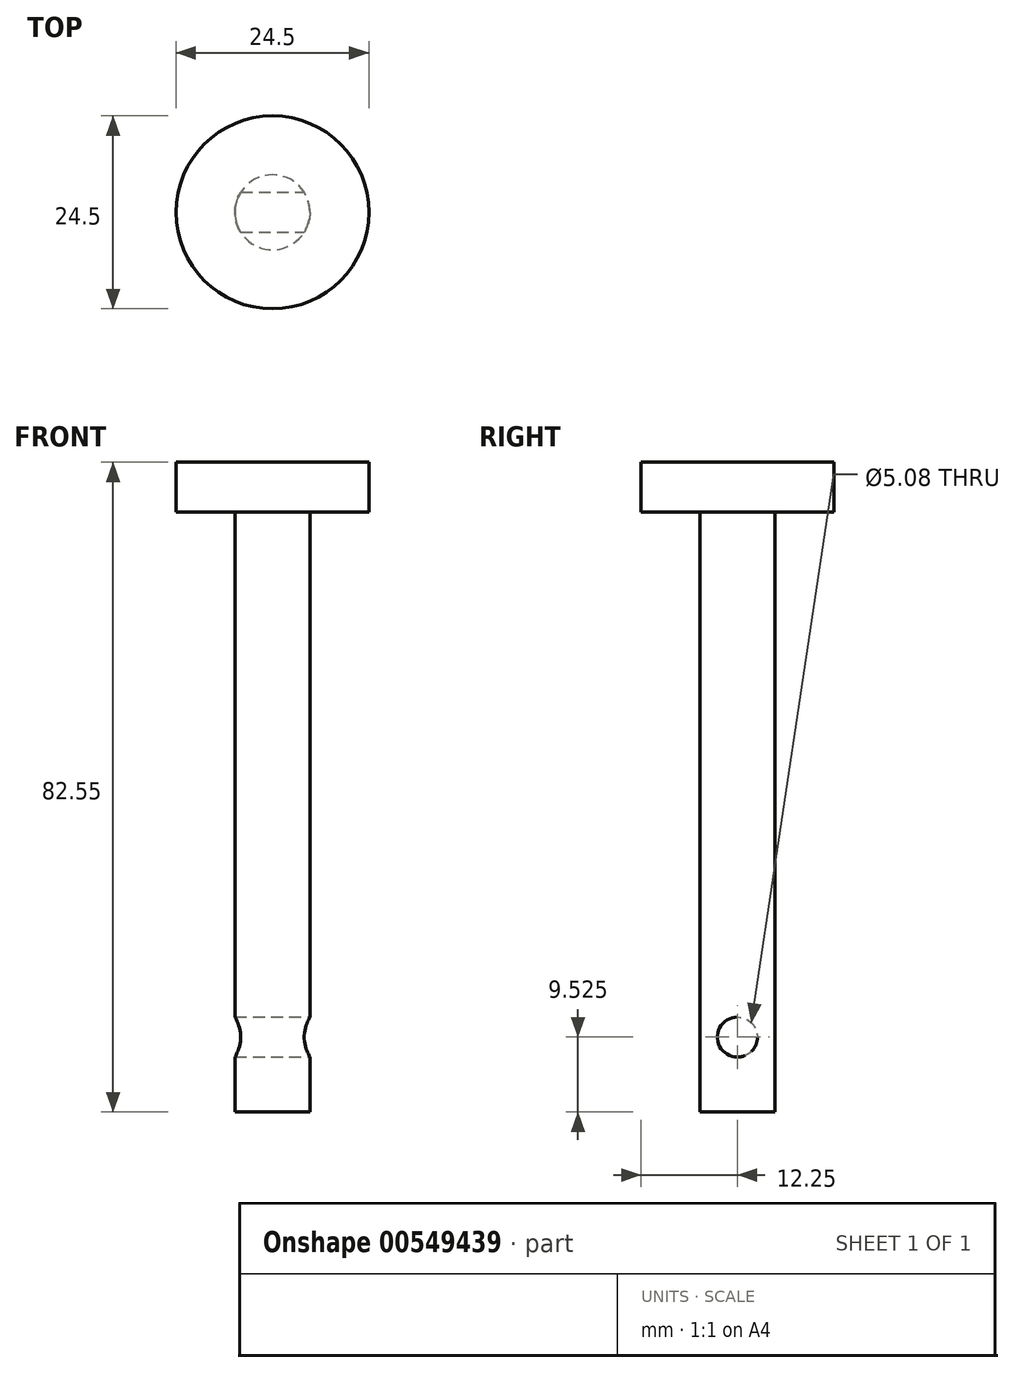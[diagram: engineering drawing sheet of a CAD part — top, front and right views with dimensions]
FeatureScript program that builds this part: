
annotation { "Feature Type Name" : "Feature", "Feature Type Description" : "" }
export const myFeature = defineFeature(function(context is Context, id is Id, definition is map)
    precondition{}
    {
        {
            var Q0;
            Q0=qCreatedBy(makeId("Right.planeOp"),FACE);
            var sketch = newSketch(context, id + "F0", { "sketchPlane" : qUnion([Q0])});
            skLineSegment(sketch, "E0.bottom", {"start": v(-4.76, 38.1) * mm, "end": v(0, 38.1) * mm});
            skLineSegment(sketch, "E0.top", {"start": v(-4.76, -38.1) * mm, "end": v(0, -38.1) * mm});
            skLineSegment(sketch, "E0.left", {"start": v(-4.76, 38.1) * mm, "end": v(-4.76, -38.1) * mm});
            skPoint(sketch, "E0.middle", {"position": v(0, 0) * mm});
            skLineSegment(sketch, "E1", {"start": v(-4.76, 38.1) * mm, "end": v(-12.25, 38.1) * mm});
            skLineSegment(sketch, "E2", {"start": v(-12.25, 38.1) * mm, "end": v(-12.25, 44.45) * mm});
            skLineSegment(sketch, "E3", {"start": v(-12.25, 44.45) * mm, "end": v(0, 44.45) * mm});
            skLineSegment(sketch, "E4", {"start": v(0, 44.45) * mm, "end": v(0, 38.1) * mm});
            skLineSegment(sketch, "E5", {"start": v(0, 44.45) * mm, "end": v(0, -38.1) * mm});
            skPoint(sketch, "E6.MirrorCS.end.orphan", {"position": v(0, 44.45) * mm});
            skPoint(sketch, "E6.MirrorCS.start.orphan", {"position": v(12.25, 44.45) * mm});
            skPoint(sketch, "E7.MirrorCS.start.orphan", {"position": v(12.25, 38.1) * mm});
            skPoint(sketch, "E0.right.start.orphan", {"position": v(4.76, 38.1) * mm});
            skPoint(sketch, "E8.orphan", {"position": v(4.76, -38.1) * mm});
            skSolve(sketch);
        }
        {
            var Q0;
            Q0 = qSketchRegion(id + "F0", true);
            var Q1;
            Q1=sQuery(id+"F0.wireOp",EDGE,"E5");
            revolve(context, id + "F1", {"surfaceOperationType" : NewSurfaceOperationType.NEW, "entities" : qUnion([Q0]), "axis" : qUnion([Q1]), "revolveType" : RevolveType.FULL});
        }
        {
            var Q0;
            Q0=qCreatedBy(makeId("Right.planeOp"),FACE);
            var sketch = newSketch(context, id + "F2", { "sketchPlane" : qUnion([Q0])});
            skCircle(sketch, "E9", {"center": v(0, -28.58) * mm, "radius": 2.54 * mm});
            skSolve(sketch);
        }
        {
            var Q0;
            Q0 = qSketchRegion(id + "F2", true);
            extrude(context, id + "F3", {"entities" : qUnion([Q0]), "operationType" : NewBodyOperationType.REMOVE, "oppositeDirection" : true, "depth" : 25.4 * mm, "offsetDistance" : 25.4 * mm, "symmetric" : true});
        }
    });
